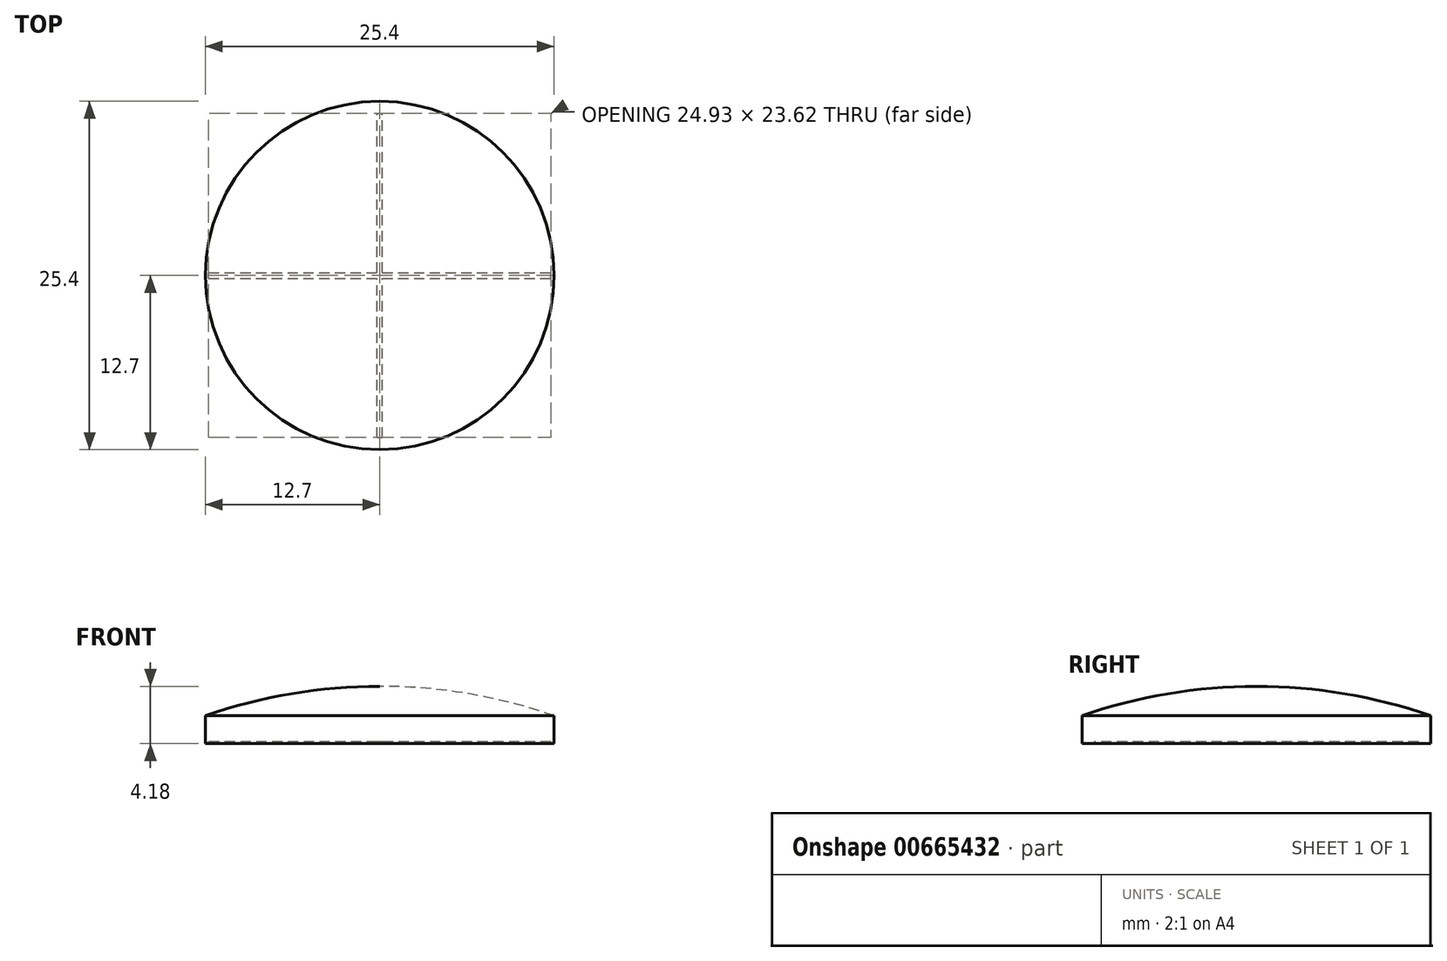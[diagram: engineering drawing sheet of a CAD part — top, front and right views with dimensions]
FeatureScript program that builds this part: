
annotation { "Feature Type Name" : "Feature", "Feature Type Description" : "" }
export const myFeature = defineFeature(function(context is Context, id is Id, definition is map)
    precondition{}
    {
        {
            var Q0;
            Q0=qCreatedBy(makeId("Front.planeOp"),FACE);
            var sketch = newSketch(context, id + "F0", { "sketchPlane" : qUnion([Q0])});
            skLineSegment(sketch, "E0.top", {"start": v(-12.7, -1.02) * mm, "end": v(0, -1.02) * mm});
            skLineSegment(sketch, "E0.left", {"start": v(-12.7, 1.02) * mm, "end": v(-12.7, -1.02) * mm});
            skPoint(sketch, "E0.middle", {"position": v(0, 0) * mm});
            skArc(sketch, "E1", {"start": v(0, 3.16) * mm, "mid": v(-6.44, 2.62) * mm, "end": v(-12.7, 1.02) * mm});
            skPoint(sketch, "E0.right.end.orphan", {"position": v(12.7, -1.02) * mm});
            skPoint(sketch, "E0.right.start.orphan", {"position": v(12.7, 1.02) * mm});
            skLineSegment(sketch, "E2", {"start": v(0, 3.16) * mm, "end": v(0, -1.02) * mm});
            skSolve(sketch);
        }
        {
            var Q0;
            Q0=makeQuery(id+"F0.imprint","IMPRINT",FACE,{"disambiguationData":[TD([[makeQuery(id+"F0.imprint","IMPRINT",EDGE,{"derivedFrom":sQuery(id+"F0.wireOp",EDGE,"E0.top")}),1.0]])]});
            var Q1;
            Q1=sQuery(id+"F0.wireOp",EDGE,"E2");
            revolve(context, id + "F1", {"surfaceOperationType" : NewSurfaceOperationType.NEW, "entities" : qUnion([Q0]), "axis" : qUnion([Q1]), "revolveType" : RevolveType.FULL});
        }
        {
            var Q0;
            Q0=makeQuery(id+"F1.opRevolve","SWEPT_FACE",FACE,{"disambiguationData":[OSD([sQuery(id+"F0.wireOp",EDGE,"E0.top")])]});
            var sketch = newSketch(context, id + "F2", { "sketchPlane" : qUnion([Q0])});
            skLineSegment(sketch, "E3.bottom", {"start": v(0.2, -11.81) * mm, "end": v(-0.2, -11.81) * mm});
            skLineSegment(sketch, "E3.top", {"start": v(0.2, 11.81) * mm, "end": v(-0.2, 11.81) * mm});
            skLineSegment(sketch, "E3.left", {"start": v(0.2, -11.81) * mm, "end": v(0.2, -0.2) * mm});
            skLineSegment(sketch, "E3.right", {"start": v(-0.2, -11.81) * mm, "end": v(-0.2, -0.2) * mm});
            skPoint(sketch, "E3.middle", {"position": v(0, 0) * mm});
            skLineSegment(sketch, "E4.bottom", {"start": v(12.47, -0.2) * mm, "end": v(0.2, -0.2) * mm});
            skLineSegment(sketch, "E4.top", {"start": v(12.47, 0.2) * mm, "end": v(0.2, 0.2) * mm});
            skLineSegment(sketch, "E4.left", {"start": v(12.47, -0.2) * mm, "end": v(12.47, 0.2) * mm});
            skLineSegment(sketch, "E4.right", {"start": v(-12.47, -0.2) * mm, "end": v(-12.47, 0.2) * mm});
            skLineSegment(sketch, "E5.trimOffspring", {"start": v(-0.2, -0.2) * mm, "end": v(-12.47, -0.2) * mm});
            skLineSegment(sketch, "E6.trimOffspring", {"start": v(-0.2, 0.2) * mm, "end": v(-0.2, 11.81) * mm});
            skLineSegment(sketch, "E7.trimOffspring", {"start": v(-0.2, 0.2) * mm, "end": v(-12.47, 0.2) * mm});
            skLineSegment(sketch, "E8.trimOffspring", {"start": v(0.2, 0.2) * mm, "end": v(0.2, 11.81) * mm});
            skSolve(sketch);
        }
        {
            var Q0;
            Q0 = qSketchRegion(id + "F2", true);
            extrude(context, id + "F3", {"entities" : qUnion([Q0]), "operationType" : NewBodyOperationType.REMOVE, "depth" : 0.25 * mm, "offsetDistance" : 25.4 * mm, "symmetric" : true});
        }
    });
